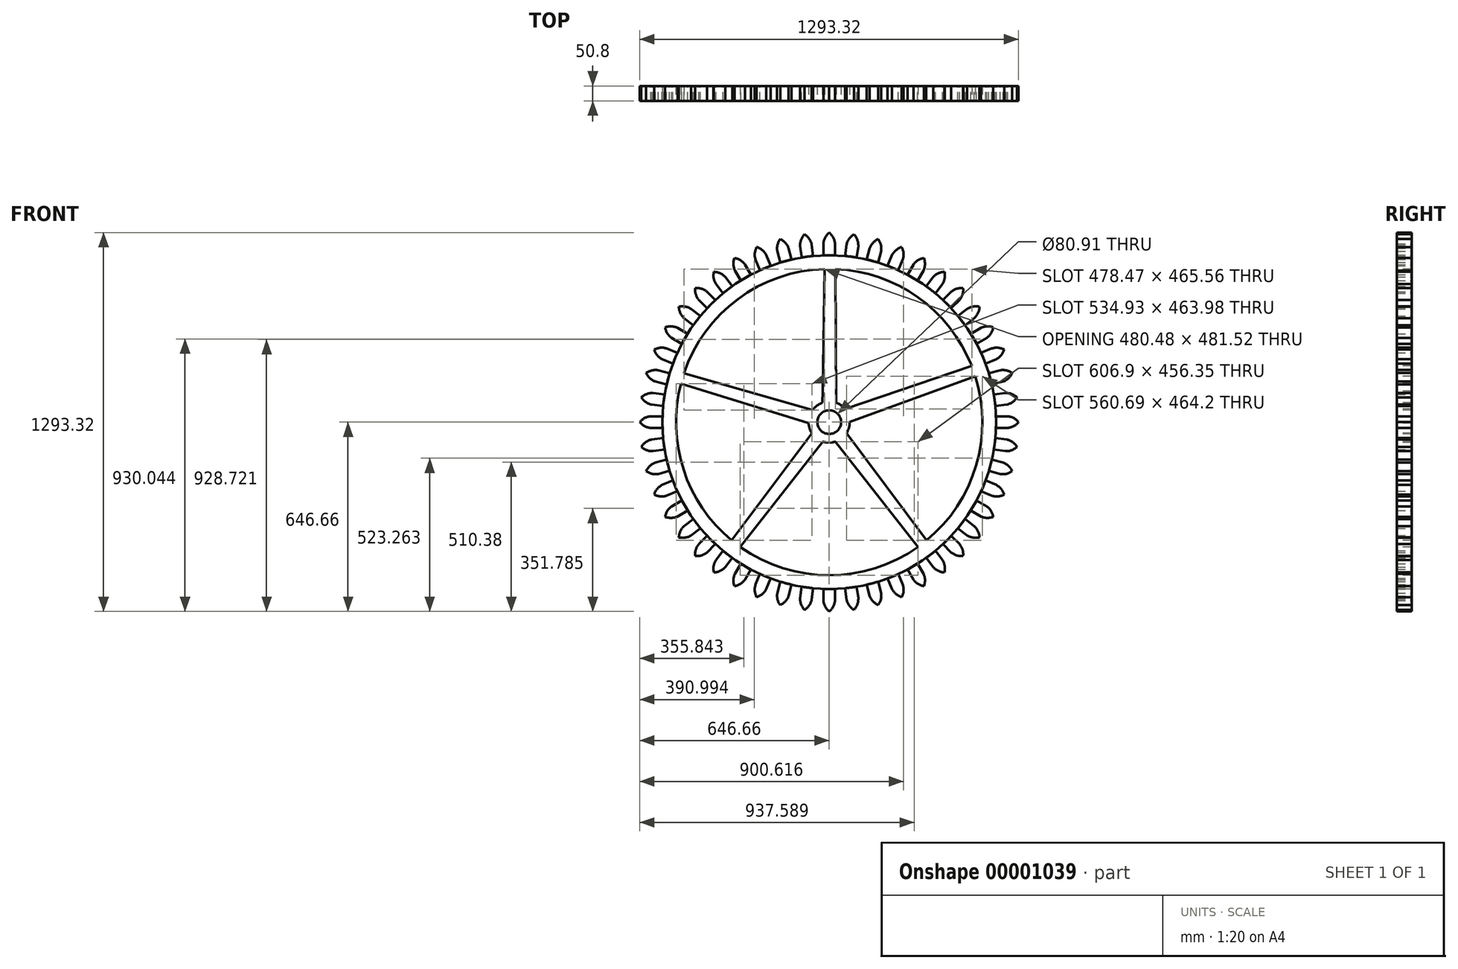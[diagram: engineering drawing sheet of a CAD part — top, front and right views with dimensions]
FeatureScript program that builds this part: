
annotation { "Feature Type Name" : "Feature", "Feature Type Description" : "" }
export const myFeature = defineFeature(function(context is Context, id is Id, definition is map)
    precondition{}
    {
        {
            var Q0;
            Q0=qCreatedBy(makeId("Front.planeOp"),FACE);
            var sketch = newSketch(context, id + "F0", { "sketchPlane" : qUnion([Q0])});
            skCircle(sketch, "E0", {"center": v(0, 0) * mm, "radius": 569.7 * mm});
            skPoint(sketch, "E1.orphan", {"position": v(0, 569.7) * mm});
            skPoint(sketch, "E2.end.orphan", {"position": v(-246.63, -176.05) * mm});
            skPoint(sketch, "E3.start.orphan", {"position": v(-146.19, -176.05) * mm});
            skPoint(sketch, "E4.orphan", {"position": v(-541.81, -176.05) * mm});
            skArc(sketch, "E5", {"start": v(-303.45, -426.03) * mm, "mid": v(0, -523.05) * mm, "end": v(303.45, -426.03) * mm});
            skArc(sketch, "E6.trimOffspring", {"start": v(-506.33, 131.18) * mm, "mid": v(-497.45, -161.63) * mm, "end": v(-332.52, -403.74) * mm});
            skArc(sketch, "E7.trimOffspring", {"start": v(-15.42, 522.82) * mm, "mid": v(-311.68, 420.04) * mm, "end": v(-495.9, 166.3) * mm});
            skArc(sketch, "E8.trimOffspring", {"start": v(332.52, -403.74) * mm, "mid": v(497.36, -161.91) * mm, "end": v(506.48, 130.61) * mm});
            skArc(sketch, "E9.trimOffspring", {"start": v(-22.45, 105.48) * mm, "mid": v(-22.47, 105.48) * mm, "end": v(-22.48, 105.48) * mm});
            skCircle(sketch, "E10", {"center": v(0, 0) * mm, "radius": 40.46 * mm});
            skLineSegment(sketch, "E11.0", {"start": v(-15.47, 521.77) * mm, "end": v(-23.14, 66.16) * mm});
            skLineSegment(sketch, "E12.0", {"start": v(-22.45, 105.48) * mm, "end": v(-15.42, 522.82) * mm});
            skLineSegment(sketch, "E13.0.MirrorCS", {"start": v(21.17, 522.62) * mm, "end": v(23.84, 65.92) * mm});
            skPoint(sketch, "E14.orphan", {"position": v(20.9, 569.31) * mm});
            skPoint(sketch, "E15.orphan", {"position": v(-14.64, 569.5) * mm});
            skPoint(sketch, "E16.orphan", {"position": v(-23.65, 34.1) * mm});
            skPoint(sketch, "E17.orphan", {"position": v(24.03, 33.84) * mm});
            skArc(sketch, "E18", {"start": v(-23.14, 66.16) * mm, "mid": v(-33.1, 61.78) * mm, "end": v(-42.27, 55.91) * mm});
            skArc(sketch, "E19.trimOffspring", {"start": v(-278.52, -442.73) * mm, "mid": v(1.3, -523.05) * mm, "end": v(280.73, -441.33) * mm});
            skArc(sketch, "E20.trimOffspring", {"start": v(486.74, 191.48) * mm, "mid": v(303.16, 426.23) * mm, "end": v(21.17, 522.62) * mm});
            skArc(sketch, "E21.trimOffspring", {"start": v(332.52, -403.74) * mm, "mid": v(501.43, -148.83) * mm, "end": v(498.95, 156.95) * mm});
            skLineSegment(sketch, "E22", {"start": v(303.16, 426.23) * mm, "end": v(0, 0) * mm, "construction": true});
            skLineSegment(sketch, "E23.0.MirrorCS", {"start": v(486.74, 191.48) * mm, "end": v(54.44, 44.15) * mm});
            skLineSegment(sketch, "E24.0.MirrorCS", {"start": v(498.95, 156.95) * mm, "end": v(70.1, -0.15) * mm});
            skArc(sketch, "E25.trimOffspring", {"start": v(54.44, 44.15) * mm, "mid": v(40.63, 57.12) * mm, "end": v(23.84, 65.92) * mm});
            skArc(sketch, "E26.trimOffspring", {"start": v(58.83, -38.11) * mm, "mid": v(67.2, -19.95) * mm, "end": v(70.1, -0.15) * mm});
            skPoint(sketch, "E27.orphan", {"position": v(497.96, 156.59) * mm});
            skLineSegment(sketch, "E28.0.MirrorCS", {"start": v(332.52, -403.74) * mm, "end": v(58.41, -37.56) * mm});
            skLineSegment(sketch, "E29.0.MirrorCS", {"start": v(0.94, -40.44) * mm, "end": v(0, -39.25) * mm});
            skPoint(sketch, "E30.orphan", {"position": v(501.43, -148.83) * mm});
            skLineSegment(sketch, "E31", {"start": v(0, -523.05) * mm, "end": v(0, 0) * mm, "construction": true});
            skLineSegment(sketch, "E32.0.MirrorCS", {"start": v(-303.45, -426.03) * mm, "end": v(-21.54, -66.7) * mm});
            skLineSegment(sketch, "E33.0.MirrorCS", {"start": v(-332.52, -403.74) * mm, "end": v(-58.41, -37.56) * mm});
            skLineSegment(sketch, "E34", {"start": v(-38.48, -12.5) * mm, "end": v(0, 0) * mm, "construction": true});
            skLineSegment(sketch, "E35.0.MirrorCS", {"start": v(-506.33, 131.18) * mm, "end": v(-69.34, -3.95) * mm});
            skLineSegment(sketch, "E36.0.MirrorCS", {"start": v(-495.9, 166.3) * mm, "end": v(-56.63, 41.3) * mm});
            skPoint(sketch, "E37.orphan", {"position": v(-497.45, -161.63) * mm});
            skArc(sketch, "E38.trimOffspring", {"start": v(-70, -3.74) * mm, "mid": v(-66.66, -21.66) * mm, "end": v(-58.83, -38.11) * mm});
            skArc(sketch, "E39.trimOffspring", {"start": v(-23.14, 66.16) * mm, "mid": v(-41.78, 56.28) * mm, "end": v(-56.63, 41.3) * mm});
            skPoint(sketch, "E40.orphan", {"position": v(22.47, -67.88) * mm});
            skArc(sketch, "E41.trimOffspring", {"start": v(-21.54, -66.7) * mm, "mid": v(0, -70.1) * mm, "end": v(21.54, -66.7) * mm});
            skPoint(sketch, "E42.orphan", {"position": v(-22.47, -67.88) * mm});
            skLineSegment(sketch, "E43.trimOffspring", {"start": v(21.54, -66.7) * mm, "end": v(303.45, -426.03) * mm});
            skPoint(sketch, "E44.orphan", {"position": v(-58.08, 41.71) * mm});
            skSolve(sketch);
        }
        {
            var Q0;
            Q0 = qSketchRegion(id + "F0", true);
            extrude(context, id + "F1", {"entities" : qUnion([Q0]), "oppositeDirection" : true, "depth" : 50.8 * mm});
        }
        {
            var Q0;
            Q0=makeQuery(id+"F1.opExtrude","CAP_FACE",FACE,{"disambiguationData":[OSD([sQuery(id+"F0.wireOp",EDGE,"E0"),sQuery(id+"F0.wireOp",EDGE,"8c9d103e-f01d-49cf-ad77-b3085b2911db"),sQuery(id+"F0.wireOp",EDGE,"b49f00f4-6076-49fc-9ce2-f03277b506f3.0.MirrorCS"),sQuery(id+"F0.wireOp",EDGE,"a2fffdda-42bf-42c0-9db8-afe848c15088.0.MirrorCS"),sQuery(id+"F0.wireOp",EDGE,"e21295ba-4559-4e5b-8803-d36e51f22ec4.0.MirrorCS"),sQuery(id+"F0.wireOp",EDGE,"b8f076f2-53f7-4fff-b40f-76b411fa6862.0.MirrorCS"),sQuery(id+"F0.wireOp",EDGE,"5fcdf7a4-7cc4-4f47-8c5c-54c51748ccaf.0.MirrorCS"),sQuery(id+"F0.wireOp",EDGE,"345fbaad-52b1-4b99-bfd0-35f4a73d1b2a.0.MirrorCS"),sQuery(id+"F0.wireOp",EDGE,"b3e473ce-852f-41b8-8e9c-44f00514d189.0.MirrorCS"),sQuery(id+"F0.wireOp",EDGE,"eb311ef3-b5d9-4ac5-898f-531d167731e8.0.MirrorCS"),sQuery(id+"F0.wireOp",EDGE,"8acb0c1c-3cf4-4cef-88ad-55272566f383.0.MirrorCS"),sQuery(id+"F0.wireOp",EDGE,"E5"),sQuery(id+"F0.wireOp",EDGE,"50cc05e8-3a40-4a5d-a07d-70cc0b0717c1"),sQuery(id+"F0.wireOp",EDGE,"E6.trimOffspring"),sQuery(id+"F0.wireOp",EDGE,"E7.trimOffspring"),sQuery(id+"F0.wireOp",EDGE,"7630990a-bb1d-4a43-90b2-d95ea90e86b9.trimOffspring"),sQuery(id+"F0.wireOp",EDGE,"E8.trimOffspring"),sQuery(id+"F0.wireOp",EDGE,"d2b266cd-91c7-443e-bf8b-d5f102a11351.trimOffspring"),sQuery(id+"F0.wireOp",EDGE,"8165a77c-8db8-4083-8ac1-8c856683f787.trimOffspring"),sQuery(id+"F0.wireOp",EDGE,"84f29ed4-df46-463d-bdd2-dc69b7ffe056.trimOffspring"),sQuery(id+"F0.wireOp",EDGE,"E9.trimOffspring"),sQuery(id+"F0.wireOp",EDGE,"E10")])],"isStart":false});
            var sketch = newSketch(context, id + "F2", { "sketchPlane" : qUnion([Q0])});
            skLineSegment(sketch, "E45.0", {"start": v(19.95, 569.35) * mm, "end": v(19.95, 609.27) * mm});
            skLineSegment(sketch, "E46.0.MirrorCS", {"start": v(-19.95, 569.35) * mm, "end": v(-19.95, 609.27) * mm});
            skCircle(sketch, "E47", {"center": v(0, 0) * mm, "radius": 609.6 * mm, "construction": true});
            skArc(sketch, "E48", {"start": v(0, 646.66) * mm, "mid": v(-13.75, 629.98) * mm, "end": v(-19.95, 609.27) * mm});
            skArc(sketch, "E49.0.MirrorCS", {"start": v(0, 646.66) * mm, "mid": v(13.75, 629.98) * mm, "end": v(19.95, 609.27) * mm});
            skPoint(sketch, "E50.orphan", {"position": v(-19.95, 646.66) * mm});
            skPoint(sketch, "E51.orphan", {"position": v(19.95, 646.66) * mm});
            skPoint(sketch, "E52.orphan", {"position": v(19.95, 0) * mm});
            skPoint(sketch, "E53.orphan", {"position": v(-19.95, 0) * mm});
            skPoint(sketch, "E54.visualSharp", {"position": v(19.95, 569.35) * mm});
            skLineSegment(sketch, "E55", {"start": v(0, 646.66) * mm, "end": v(0, -40.46) * mm});
            skArc(sketch, "E56.0", {"start": v(19.95, 569.35) * mm, "mid": v(0, 569.7) * mm, "end": v(-19.95, 569.35) * mm});
            skSolve(sketch);
        }
        {
            var Q0;
            Q0=makeQuery(id+"F2.imprint","IMPRINT",FACE,{"disambiguationData":[TD([[makeQuery(id+"F2.imprint","IMPRINT",EDGE,{"derivedFrom":sQuery(id+"F2.wireOp",EDGE,"E45.0")}),1.0]])]});
            var Q1;
            Q1=makeQuery(id+"F2.imprint","IMPRINT",FACE,{"disambiguationData":[TD([[makeQuery(id+"F2.imprint","IMPRINT",EDGE,{"derivedFrom":sQuery(id+"F2.wireOp",EDGE,"E46.0.MirrorCS")}),-1.0]])]});
            var Q2;
            Q2=sQuery(id+"F2.wireOp",EDGE,"E49.0.MirrorCS");
            var Q3;
            Q3=sQuery(id+"F2.wireOp",EDGE,"E48");
            var Q4;
            Q4=sQuery(id+"F2.wireOp",EDGE,"E46.0.MirrorCS");
            var Q5;
            Q5=sQuery(id+"F2.wireOp",EDGE,"6876474e-e487-47d3-b360-4724d9ae3969.0");
            extrude(context, id + "F3", {"entities" : qUnion([Q0, Q1]), "surfaceEntities" : qUnion([Q2, Q3, Q4, Q5]), "oppositeDirection" : true, "depth" : 50.8 * mm});
        }
        {
            var Q0;
            Q0=qCreatedBy(makeId("Right.planeOp"),FACE);
            var sketch = newSketch(context, id + "F4", { "sketchPlane" : qUnion([Q0])});
            skLineSegment(sketch, "E57", {"start": v(0, 0) * mm, "end": v(87.01, 0) * mm});
            skSolve(sketch);
        }
        {
            var Q0;
            Q0=makeQuery(id+"F3.opExtrude","CAP_FACE",FACE,{"disambiguationData":[OSD([sQuery(id+"F2.wireOp",EDGE,"E45.0"),sQuery(id+"F2.wireOp",EDGE,"E46.0.MirrorCS"),sQuery(id+"F2.wireOp",EDGE,"E48"),sQuery(id+"F2.wireOp",EDGE,"E49.0.MirrorCS"),sQuery(id+"F2.wireOp",EDGE,"E56.0")])],"isStart":false});
            var Q1;
            Q1=makeQuery(id+"F3.opExtrude","SWEPT_FACE",FACE,{"disambiguationData":[OSD([sQuery(id+"F2.wireOp",EDGE,"E48")])]});
            var Q2;
            Q2=makeQuery(id+"F3.opExtrude","SWEPT_FACE",FACE,{"disambiguationData":[OSD([sQuery(id+"F2.wireOp",EDGE,"E46.0.MirrorCS")])]});
            var Q3;
            Q3=makeQuery(id+"F3.opExtrude","CAP_FACE",FACE,{"disambiguationData":[OSD([sQuery(id+"F2.wireOp",EDGE,"E45.0"),sQuery(id+"F2.wireOp",EDGE,"E46.0.MirrorCS"),sQuery(id+"F2.wireOp",EDGE,"E48"),sQuery(id+"F2.wireOp",EDGE,"E49.0.MirrorCS"),sQuery(id+"F2.wireOp",EDGE,"E56.0")])],"isStart":true});
            var Q4;
            Q4=makeQuery(id+"F3.opExtrude","SWEPT_FACE",FACE,{"disambiguationData":[OSD([sQuery(id+"F2.wireOp",EDGE,"E45.0")])]});
            var Q5;
            Q5=makeQuery(id+"F3.opExtrude","SWEPT_FACE",FACE,{"disambiguationData":[OSD([sQuery(id+"F2.wireOp",EDGE,"E49.0.MirrorCS")])]});
            var Q6;
            Q6=makeQuery(id+"F3.opExtrude","SWEPT_BODY",BODY,{"disambiguationData":[OSD([sQuery(id+"F2.wireOp",EDGE,"E45.0"),sQuery(id+"F2.wireOp",EDGE,"E46.0.MirrorCS"),sQuery(id+"F2.wireOp",EDGE,"E48"),sQuery(id+"F2.wireOp",EDGE,"E49.0.MirrorCS"),sQuery(id+"F2.wireOp",EDGE,"E56.0")])]});
            var Q7;
            Q7=sQuery(id+"F4.wireOp",EDGE,"E57");
            circularPattern(context, id + "F5", {"entities" : qUnion([Q6]), "axis" : qUnion([Q7]), "angle" : 360 * degree, "instanceCount" : 48, "equalSpace" : true});
        }
        {
            var Q0;
            Q0=makeQuery(id+"F5.opPattern","COPY",EDGE,{"derivedFrom":makeQuery(id+"F3.opExtrude","SWEPT_EDGE",EDGE,{"disambiguationData":[OSD([sQuery(id+"F0.wireOp",EDGE,"E0"),sQuery(id+"F2.wireOp",EDGE,"E46.0.MirrorCS"),sQuery(id+"F2.wireOp",EDGE,"E56.0")])]}),"instanceName":"46"});
            var Q1;
            Q1=makeQuery(id+"F5.opPattern","COPY",EDGE,{"derivedFrom":makeQuery(id+"F3.opExtrude","SWEPT_EDGE",EDGE,{"disambiguationData":[OSD([sQuery(id+"F0.wireOp",EDGE,"E0"),sQuery(id+"F2.wireOp",EDGE,"E45.0"),sQuery(id+"F2.wireOp",EDGE,"E56.0")])]}),"instanceName":"47"});
            fillet(context, id + "F6", {"entities" : qUnion([Q0, Q1]), "radius" : 5.08 * mm, "tangentPropagation" : true, "allowEdgeOverflow" : false});
        }
    });
